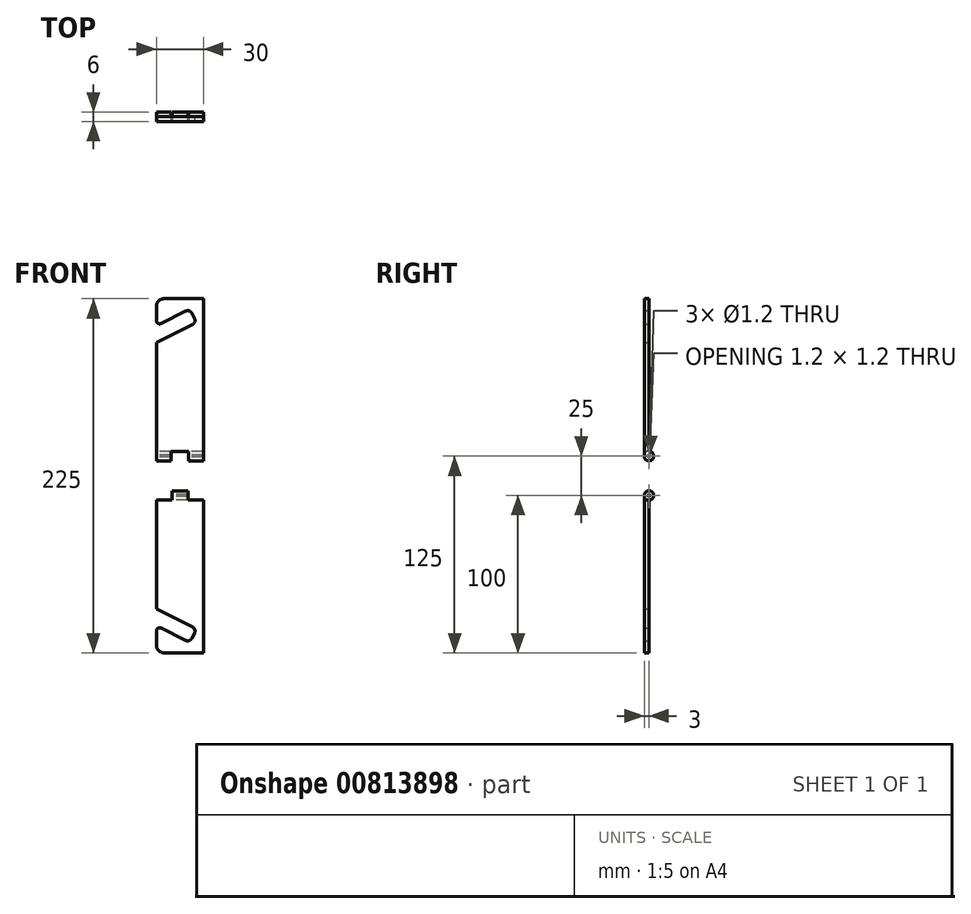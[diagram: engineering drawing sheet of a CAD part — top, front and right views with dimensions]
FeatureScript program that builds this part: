
annotation { "Feature Type Name" : "Feature", "Feature Type Description" : "" }
export const myFeature = defineFeature(function(context is Context, id is Id, definition is map)
    precondition{}
    {
        {
            var Q0;
            Q0=qCreatedBy(makeId("Front.planeOp"),FACE);
            var sketch = newSketch(context, id + "F0", { "sketchPlane" : qUnion([Q0])});
            skLineSegment(sketch, "E0.bottom", {"start": v(5, 52.5) * mm, "end": v(30, 52.5) * mm});
            skLineSegment(sketch, "E0.top", {"start": v(0, -47.5) * mm, "end": v(30, -47.5) * mm});
            skLineSegment(sketch, "E0.left", {"start": v(0, 47.5) * mm, "end": v(0, 38.52) * mm});
            skLineSegment(sketch, "E1.trimOffspring", {"start": v(30, 52.5) * mm, "end": v(30, -47.5) * mm});
            skLineSegment(sketch, "E2", {"start": v(2.89, 36.72) * mm, "end": v(18.6, 44.52) * mm});
            skLineSegment(sketch, "E3", {"start": v(22.62, 43.17) * mm, "end": v(24.2, 39.98) * mm});
            skLineSegment(sketch, "E4", {"start": v(22.85, 35.96) * mm, "end": v(0, 24.6) * mm});
            skPoint(sketch, "E5.visualSharp", {"position": v(0, 52.5) * mm});
            skArc(sketch, "E5.filletArc", {"start": v(5, 52.5) * mm, "mid": v(1.46, 51.04) * mm, "end": v(0, 47.5) * mm});
            skLineSegment(sketch, "E6.trimOffspring", {"start": v(0, 24.6) * mm, "end": v(0, -47.5) * mm});
            skPoint(sketch, "E7.visualSharp", {"position": v(0, 35.29) * mm});
            skArc(sketch, "E7.filletArc", {"start": v(0, 38.52) * mm, "mid": v(0.95, 36.82) * mm, "end": v(2.89, 36.72) * mm});
            skPoint(sketch, "E8.visualSharp", {"position": v(21.28, 45.86) * mm});
            skArc(sketch, "E8.filletArc", {"start": v(22.62, 43.17) * mm, "mid": v(20.88, 44.68) * mm, "end": v(18.6, 44.52) * mm});
            skPoint(sketch, "E9.visualSharp", {"position": v(25.54, 37.3) * mm});
            skArc(sketch, "E9.filletArc", {"start": v(22.85, 35.96) * mm, "mid": v(24.36, 37.69) * mm, "end": v(24.2, 39.98) * mm});
            skSolve(sketch);
        }
        {
            var Q0;
            Q0=makeQuery(id+"F0.imprint","IMPRINT",FACE,{"disambiguationData":[TD([[makeQuery(id+"F0.imprint","IMPRINT",EDGE,{"derivedFrom":sQuery(id+"F0.wireOp",EDGE,"E0.bottom")}),-1.0]])]});
            extrude(context, id + "F1", {"entities" : qUnion([Q0]), "endBound" : BoundingType.SYMMETRIC, "depth" : 3 * mm, "offsetDistance" : 25 * mm});
        }
        {
            var Q0;
            Q0=qCreatedBy(makeId("Right.planeOp"),FACE);
            var sketch = newSketch(context, id + "F2", { "sketchPlane" : qUnion([Q0])});
            skCircle(sketch, "E10", {"center": v(1.5, -47.5) * mm, "radius": 3 * mm});
            skCircle(sketch, "E11", {"center": v(1.5, -47.5) * mm, "radius": 0.6 * mm});
            skLineSegment(sketch, "E12", {"start": v(1.5, 24.6) * mm, "end": v(1.5, -47.5) * mm});
            skLineSegment(sketch, "E13", {"start": v(-1.5, 24.6) * mm, "end": v(1.5, 24.6) * mm});
            skLineSegment(sketch, "E14", {"start": v(-1.5, 24.6) * mm, "end": v(-1.5, -47.5) * mm});
            skLineSegment(sketch, "E15", {"start": v(-1.5, -47.5) * mm, "end": v(1.5, -47.5) * mm});
            skSolve(sketch);
        }
        {
            var Q0;
            Q0 = qSketchRegion(id + "F2", true);
            extrude(context, id + "F3", {"entities" : qUnion([Q0]), "operationType" : NewBodyOperationType.ADD, "depth" : 30 * mm, "offsetDistance" : 25 * mm});
        }
        {
            var Q0;
            {var subQ0=sQuery(id+"F2.wireOp",EDGE,"E12");var subQ1=sQuery(id+"F2.wireOp",EDGE,"E11");var subQ2=makeQuery(id+"F2.imprint","INTERSECT",VERTEX,{"derivedFrom":[subQ1,subQ0]});Q0=makeQuery(id+"F2.imprint","IMPRINT",FACE,{"disambiguationData":[TD([[makeQuery(id+"F2.imprint","IMPRINT",EDGE,{"disambiguationData":[TD([[subQ2,-1.0]])],"derivedFrom":subQ1}),1.0]])]});}
            extrude(context, id + "F4", {"entities" : qUnion([Q0]), "operationType" : NewBodyOperationType.REMOVE, "depth" : 30 * mm, "offsetDistance" : 25 * mm});
        }
        {
            var Q0;
            Q0=qCreatedBy(makeId("Top.planeOp"),FACE);
            cPlane(context, id + "F5", {"entities" : qUnion([Q0]), "cplaneType" : CPlaneType.OFFSET, "offset" : 60 * mm, "oppositeDirection" : true, "width" : 150 * mm, "height" : 150 * mm});
        }
        {
            var Q0;
            Q0=makeQuery(id+"F1.opExtrude","SWEPT_BODY",BODY,{"disambiguationData":[OSD([sQuery(id+"F0.wireOp",EDGE,"E0.bottom"),sQuery(id+"F0.wireOp",EDGE,"E0.top"),sQuery(id+"F0.wireOp",EDGE,"E0.left"),sQuery(id+"F0.wireOp",EDGE,"E0.right"),sQuery(id+"F0.wireOp",EDGE,"104f33cd-b7b7-41f1-8374-5aee490c37a0.filletArc"),sQuery(id+"F0.wireOp",EDGE,"kghCvj7r-sTSC-CnFG-uqwU-uWBLIQd3OtcP"),sQuery(id+"F0.wireOp",EDGE,"KBjbeXU5-Sf9Q-N5gx-Wwxf-5VQjuIYt9WiE"),sQuery(id+"F0.wireOp",EDGE,"mb3XriJl-V7Ix-f0ng-Q0kY-46K9PvjHQxnH"),sQuery(id+"F0.wireOp",EDGE,"E1.trimOffspring"),sQuery(id+"F0.wireOp",EDGE,"085e8f33-6bec-45d6-8575-eebe7561a367.filletArc"),sQuery(id+"F0.wireOp",EDGE,"3d77ea6d-f4f6-45e5-95e1-abb230e23f9e.filletArc"),sQuery(id+"F0.wireOp",EDGE,"e216d516-8039-4250-9782-b2dc57d9e46a.filletArc")])]});
            var Q1;
            Q1=qCreatedBy(id+"F5.planeOp",FACE);
            mirror(context, id + "F6", {"entities" : qUnion([Q0]), "mirrorPlane" : qUnion([Q1])});
        }
        {
            var Q0;
            Q0=qCreatedBy(makeId("Front.planeOp"),FACE);
            var sketch = newSketch(context, id + "F7", { "sketchPlane" : qUnion([Q0])});
            skLineSegment(sketch, "E16", {"start": v(9.5, -44.5) * mm, "end": v(9.5, -50.5) * mm});
            skLineSegment(sketch, "E17", {"start": v(20.5, -44.5) * mm, "end": v(20.5, -50.5) * mm});
            skLineSegment(sketch, "E18", {"start": v(20.5, -50.5) * mm, "end": v(9.5, -50.5) * mm});
            skLineSegment(sketch, "E19", {"start": v(9.5, -44.5) * mm, "end": v(20.5, -44.5) * mm});
            skSolve(sketch);
        }
        {
            var Q0;
            Q0 = qSketchRegion(id + "F7", true);
            extrude(context, id + "F8", {"entities" : qUnion([Q0]), "operationType" : NewBodyOperationType.REMOVE, "endBound" : BoundingType.SYMMETRIC, "oppositeDirection" : true, "depth" : 14 * mm, "offsetDistance" : 25 * mm});
        }
        {
            var Q0;
            Q0=qCreatedBy(makeId("Front.planeOp"),FACE);
            var sketch = newSketch(context, id + "F9", { "sketchPlane" : qUnion([Q0])});
            skLineSegment(sketch, "E20.bottom", {"start": v(0, -69.5) * mm, "end": v(10, -69.5) * mm});
            skLineSegment(sketch, "E20.top", {"start": v(0, -75.5) * mm, "end": v(10, -75.5) * mm});
            skLineSegment(sketch, "E20.left", {"start": v(0, -69.5) * mm, "end": v(0, -75.5) * mm});
            skLineSegment(sketch, "E20.right", {"start": v(10, -69.5) * mm, "end": v(10, -75.5) * mm});
            skSolve(sketch);
        }
        {
            var Q0;
            Q0 = qSketchRegion(id + "F9", true);
            extrude(context, id + "F10", {"entities" : qUnion([Q0]), "operationType" : NewBodyOperationType.REMOVE, "endBound" : BoundingType.SYMMETRIC, "depth" : 25 * mm, "offsetDistance" : 25 * mm});
        }
        {
            var Q0;
            Q0=qCreatedBy(makeId("Front.planeOp"),FACE);
            var sketch = newSketch(context, id + "F11", { "sketchPlane" : qUnion([Q0])});
            skLineSegment(sketch, "E21.bottom", {"start": v(20, -69.5) * mm, "end": v(30, -69.5) * mm});
            skLineSegment(sketch, "E21.top", {"start": v(20, -75.5) * mm, "end": v(30, -75.5) * mm});
            skLineSegment(sketch, "E21.left", {"start": v(20, -69.5) * mm, "end": v(20, -75.5) * mm});
            skLineSegment(sketch, "E21.right", {"start": v(30, -69.5) * mm, "end": v(30, -75.5) * mm});
            skSolve(sketch);
        }
        {
            var Q0;
            Q0 = qSketchRegion(id + "F11", true);
            extrude(context, id + "F12", {"entities" : qUnion([Q0]), "operationType" : NewBodyOperationType.REMOVE, "endBound" : BoundingType.SYMMETRIC, "depth" : 25 * mm, "offsetDistance" : 25 * mm});
        }
    });
